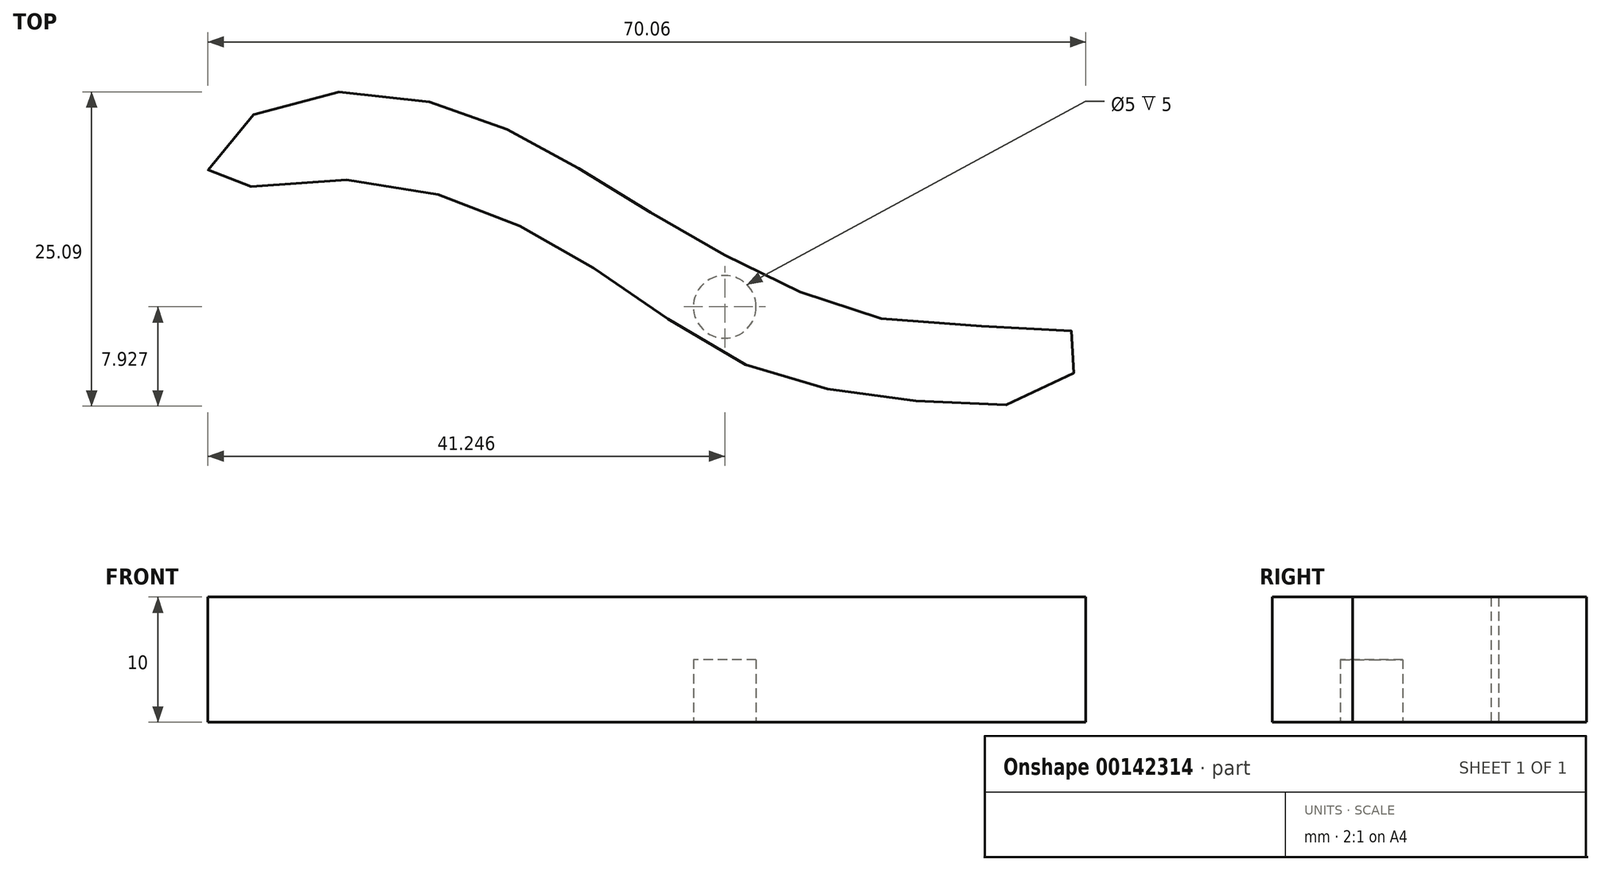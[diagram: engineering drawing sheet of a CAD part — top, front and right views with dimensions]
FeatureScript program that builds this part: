
annotation { "Feature Type Name" : "Feature", "Feature Type Description" : "" }
export const myFeature = defineFeature(function(context is Context, id is Id, definition is map)
    precondition{}
    {
        {
            var Q0;
            Q0=qCreatedBy(makeId("Top.planeOp"),FACE);
            var sketch = newSketch(context, id + "F0", { "sketchPlane" : qUnion([Q0])});
            skFitSpline(sketch, "E0", {"points": [v(-78.25, 5.2) * mm, v(-65.7, 6.55) * mm, v(-55.54, 2.8) * mm, v(-45.92, -2.97) * mm, v(-35.77, -8.42) * mm, v(-23.75, -11.62) * mm, v(-12, -12.69) * mm, v(-14.67, -16.96) * mm, v(-26.42, -17.5) * mm, v(-38.18, -15.1) * mm, v(-49.21, -8.28) * mm, v(-59.55, -2.54) * mm, v(-72.64, 0) * mm, v(-81.72, 0) * mm, v(-78.25, 5.2) * mm]});
            skSolve(sketch);
        }
        {
            var Q0;
            Q0 = qSketchRegion(id + "F0", true);
            extrude(context, id + "F1", {"entities" : qUnion([Q0]), "depth" : 10 * mm});
        }
        {
            var Q0;
            Q0=qCreatedBy(makeId("Top.planeOp"),FACE);
            var sketch = newSketch(context, id + "F2", { "sketchPlane" : qUnion([Q0])});
            skCircle(sketch, "E1", {"center": v(-40.62, -10.12) * mm, "radius": 2.5 * mm});
            skSolve(sketch);
        }
        {
            var Q0;
            Q0 = qSketchRegion(id + "F2", true);
            extrude(context, id + "F3", {"entities" : qUnion([Q0]), "operationType" : NewBodyOperationType.REMOVE, "depth" : 5 * mm});
        }
    });
